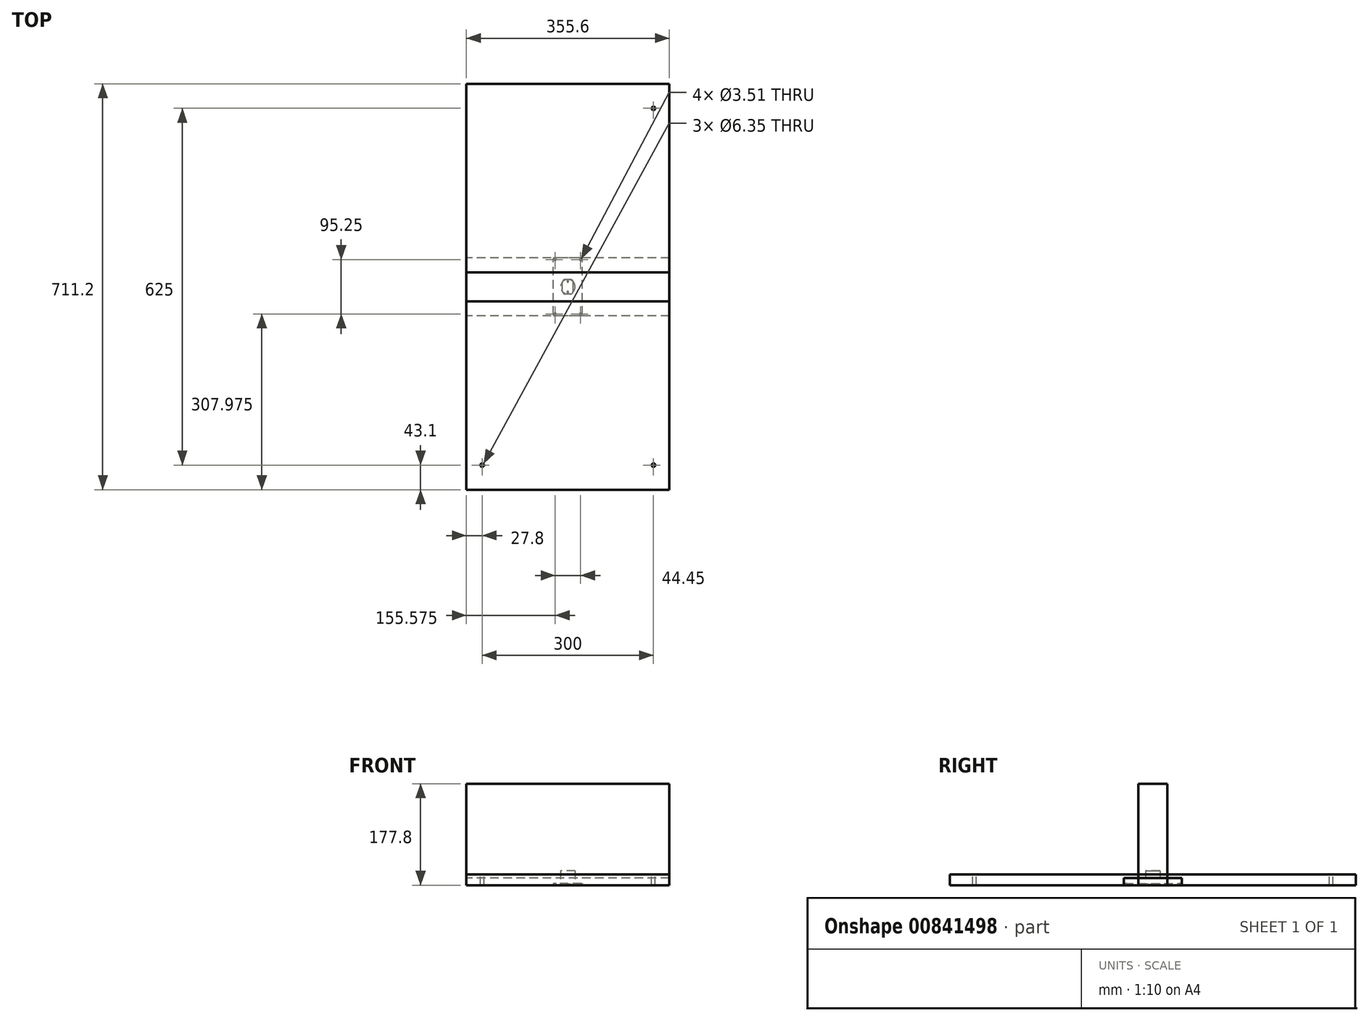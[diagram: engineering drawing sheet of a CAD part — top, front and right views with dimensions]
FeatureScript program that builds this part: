
annotation { "Feature Type Name" : "Feature", "Feature Type Description" : "" }
export const myFeature = defineFeature(function(context is Context, id is Id, definition is map)
    precondition{}
    {
        {
            var Q0;
            Q0=qCreatedBy(makeId("Top.planeOp"),FACE);
            var sketch = newSketch(context, id + "F0", { "sketchPlane" : qUnion([Q0])});
            skLineSegment(sketch, "E0.bottom", {"start": v(177.8, -355.6) * mm, "end": v(-177.8, -355.6) * mm});
            skLineSegment(sketch, "E0.top", {"start": v(177.8, 355.6) * mm, "end": v(-177.8, 355.6) * mm});
            skLineSegment(sketch, "E0.left", {"start": v(177.8, -355.6) * mm, "end": v(177.8, 355.6) * mm});
            skLineSegment(sketch, "E0.right", {"start": v(-177.8, -355.6) * mm, "end": v(-177.8, 355.6) * mm});
            skPoint(sketch, "E0.middle", {"position": v(0, 0) * mm});
            skSolve(sketch);
        }
        {
            var Q0;
            Q0=qSketchRegion(id+"F0",true);
            extrude(context, id + "F1", {"entities" : qUnion([Q0]), "depth" : 19.05 * mm, "offsetDistance" : 25.4 * mm});
        }
        {
            var Q0;
            Q0=qCreatedBy(makeId("Top.planeOp"),FACE);
            var sketch = newSketch(context, id + "F2", { "sketchPlane" : qUnion([Q0])});
            skLineSegment(sketch, "E1.bottom", {"start": v(177.8, -25.4) * mm, "end": v(-177.8, -25.4) * mm});
            skLineSegment(sketch, "E1.top", {"start": v(177.8, 25.4) * mm, "end": v(-177.8, 25.4) * mm});
            skLineSegment(sketch, "E1.left", {"start": v(177.8, -25.4) * mm, "end": v(177.8, 25.4) * mm});
            skLineSegment(sketch, "E1.right", {"start": v(-177.8, -25.4) * mm, "end": v(-177.8, 25.4) * mm});
            skPoint(sketch, "E1.middle", {"position": v(0, 0) * mm});
            skSolve(sketch);
        }
        {
            var Q0;
            Q0=qSketchRegion(id+"F2",true);
            extrude(context, id + "F3", {"entities" : qUnion([Q0]), "depth" : 177.8 * mm, "offsetDistance" : 25.4 * mm});
        }
        {
            var Q0;
            Q0=qCreatedBy(makeId("Top.planeOp"),FACE);
            var sketch = newSketch(context, id + "F4", { "sketchPlane" : qUnion([Q0])});
            skLineSegment(sketch, "E2.bottom", {"start": v(177.8, -50.8) * mm, "end": v(-177.8, -50.8) * mm});
            skLineSegment(sketch, "E2.top", {"start": v(177.8, 50.8) * mm, "end": v(-177.8, 50.8) * mm});
            skLineSegment(sketch, "E2.left", {"start": v(177.8, -50.8) * mm, "end": v(177.8, 50.8) * mm});
            skLineSegment(sketch, "E2.right", {"start": v(-177.8, -50.8) * mm, "end": v(-177.8, 50.8) * mm});
            skPoint(sketch, "E2.middle", {"position": v(0, 0) * mm});
            skSolve(sketch);
        }
        {
            var Q0;
            Q0=qSketchRegion(id+"F4",true);
            extrude(context, id + "F5", {"entities" : qUnion([Q0]), "depth" : 12.7 * mm, "offsetDistance" : 25.4 * mm});
        }
        {
            var Q0;
            Q0=qCreatedBy(makeId("Top.planeOp"),FACE);
            var sketch = newSketch(context, id + "F6", { "sketchPlane" : qUnion([Q0])});
            skCircle(sketch, "E3", {"center": v(0, 0) * mm, "radius": 12.7 * mm});
            skSolve(sketch);
        }
        {
            var Q0;
            Q0=qSketchRegion(id+"F6",true);
            extrude(context, id + "F7", {"entities" : qUnion([Q0]), "depth" : 25.4 * mm, "offsetDistance" : 25.4 * mm});
        }
        {
            var Q0;
            Q0=makeQuery(id+"F1.opExtrude","CAP_FACE",FACE,{"disambiguationData":[OSD([sQuery(id+"F0.wireOp",EDGE,"E0.bottom"),sQuery(id+"F0.wireOp",EDGE,"E0.top"),sQuery(id+"F0.wireOp",EDGE,"E0.left"),sQuery(id+"F0.wireOp",EDGE,"E0.right")])],"isStart":false});
            var sketch = newSketch(context, id + "F8", { "sketchPlane" : qUnion([Q0])});
            skLineSegment(sketch, "E4.bottom", {"start": v(150, 312.5) * mm, "end": v(-150, 312.5) * mm, "construction": true});
            skLineSegment(sketch, "E4.top", {"start": v(150, -312.5) * mm, "end": v(-150, -312.5) * mm, "construction": true});
            skLineSegment(sketch, "E4.left", {"start": v(150, 312.5) * mm, "end": v(150, -312.5) * mm, "construction": true});
            skLineSegment(sketch, "E4.right", {"start": v(-150, 312.5) * mm, "end": v(-150, -312.5) * mm, "construction": true});
            skPoint(sketch, "E4.middle", {"position": v(0, 0) * mm});
            skSolve(sketch);
        }
        {
            var Q0;
            Q0=sQuery(id+"F8.wireOp",VERTEX,"E4.top.end");
            var Q1;
            Q1=sQuery(id+"F8.wireOp",VERTEX,"E4.top.start");
            var Q2;
            Q2=sQuery(id+"F8.wireOp",VERTEX,"E4.bottom.start");
            var Q3;
            Q3=makeQuery(id+"F1.opExtrude","SWEPT_BODY",BODY,{"disambiguationData":[OSD([sQuery(id+"F0.wireOp",EDGE,"E0.bottom"),sQuery(id+"F0.wireOp",EDGE,"E0.top"),sQuery(id+"F0.wireOp",EDGE,"E0.left"),sQuery(id+"F0.wireOp",EDGE,"E0.right")])]});
            hole(context, id + "F9", {"style" : HoleStyle.SIMPLE, "endStyle" : HoleEndStyle.THROUGH, "holeDiameter" : 6.35 * mm, "majorDiameter" : 6.35 * mm, "isTappedThrough" : true, "tappedDepth" : 12.7 * mm, "tapClearance" : 3, "locations" : qUnion([Q0, Q1, Q2]), "scope" : qUnion([Q3])});
        }
        {
            var Q0;
            Q0=qSketchRegion(id+"F0",true);
            var sketch = newSketch(context, id + "F10", { "sketchPlane" : qUnion([Q0])});
            skLineSegment(sketch, "E5.bottom", {"start": v(25.4, -50.8) * mm, "end": v(-25.4, -50.8) * mm});
            skLineSegment(sketch, "E5.top", {"start": v(25.4, 50.8) * mm, "end": v(-25.4, 50.8) * mm});
            skLineSegment(sketch, "E5.left", {"start": v(25.4, -50.8) * mm, "end": v(25.4, 50.8) * mm});
            skLineSegment(sketch, "E5.right", {"start": v(-25.4, -50.8) * mm, "end": v(-25.4, 50.8) * mm});
            skPoint(sketch, "E5.middle", {"position": v(0, 0) * mm});
            skSolve(sketch);
        }
        {
            var Q0;
            Q0=qSketchRegion(id+"F10",true);
            extrude(context, id + "F11", {"entities" : qUnion([Q0]), "depth" : 3.17 * mm, "offsetDistance" : 25.4 * mm});
        }
        {
            var Q0;
            Q0=makeQuery(id+"F11.opExtrude","SWEPT_EDGE",EDGE,{"disambiguationData":[OSD([sQuery(id+"F10.wireOp",EDGE,"E5.bottom"),sQuery(id+"F10.wireOp",EDGE,"E5.left")])]});
            var Q1;
            Q1=makeQuery(id+"F11.opExtrude","SWEPT_EDGE",EDGE,{"disambiguationData":[OSD([sQuery(id+"F10.wireOp",EDGE,"E5.bottom"),sQuery(id+"F10.wireOp",EDGE,"E5.right")])]});
            var Q2;
            Q2=makeQuery(id+"F11.opExtrude","SWEPT_EDGE",EDGE,{"disambiguationData":[OSD([sQuery(id+"F10.wireOp",EDGE,"E5.top"),sQuery(id+"F10.wireOp",EDGE,"E5.left")])]});
            var Q3;
            Q3=makeQuery(id+"F11.opExtrude","SWEPT_EDGE",EDGE,{"disambiguationData":[OSD([sQuery(id+"F10.wireOp",EDGE,"E5.top"),sQuery(id+"F10.wireOp",EDGE,"E5.right")])]});
            fillet(context, id + "F12", {"entities" : qUnion([Q0, Q1, Q2, Q3]), "radius" : 1.59 * mm, "tangentPropagation" : true, "allowEdgeOverflow" : false});
        }
        {
            var Q0;
            Q0=makeQuery(id+"F11.opExtrude","CAP_FACE",FACE,{"disambiguationData":[OSD([sQuery(id+"F10.wireOp",EDGE,"E5.bottom"),sQuery(id+"F10.wireOp",EDGE,"E5.top"),sQuery(id+"F10.wireOp",EDGE,"E5.left"),sQuery(id+"F10.wireOp",EDGE,"E5.right")])],"isStart":false});
            var sketch = newSketch(context, id + "F13", { "sketchPlane" : qUnion([Q0])});
            skLineSegment(sketch, "E6.bottom", {"start": v(-22.23, -47.62) * mm, "end": v(22.23, -47.62) * mm});
            skLineSegment(sketch, "E6.top", {"start": v(-22.23, 47.62) * mm, "end": v(22.23, 47.62) * mm});
            skLineSegment(sketch, "E6.left", {"start": v(-22.23, -47.62) * mm, "end": v(-22.23, 47.62) * mm});
            skLineSegment(sketch, "E6.right", {"start": v(22.23, -47.62) * mm, "end": v(22.23, 47.62) * mm});
            skPoint(sketch, "E6.middle", {"position": v(0, 0) * mm});
            skSolve(sketch);
        }
        {
            var Q0;
            Q0=sQuery(id+"F13.wireOp",VERTEX,"E6.bottom.end");
            var Q1;
            Q1=sQuery(id+"F13.wireOp",VERTEX,"E6.bottom.start");
            var Q2;
            Q2=sQuery(id+"F13.wireOp",VERTEX,"E6.left.end");
            var Q3;
            Q3=sQuery(id+"F13.wireOp",VERTEX,"E6.top.end");
            var Q4;
            Q4=makeQuery(id+"F11.opExtrude","SWEPT_BODY",BODY,{"disambiguationData":[OSD([sQuery(id+"F10.wireOp",EDGE,"E5.bottom"),sQuery(id+"F10.wireOp",EDGE,"E5.top"),sQuery(id+"F10.wireOp",EDGE,"E5.left"),sQuery(id+"F10.wireOp",EDGE,"E5.right")])]});
            hole(context, id + "F14", {"style" : HoleStyle.SIMPLE, "endStyle" : HoleEndStyle.THROUGH, "holeDiameter" : 3.5 * mm, "majorDiameter" : 6.35 * mm, "isTappedThrough" : true, "tappedDepth" : 12.7 * mm, "tapClearance" : 3, "locations" : qUnion([Q0, Q1, Q2, Q3]), "scope" : qUnion([Q4])});
        }
        {
            var Q0;
            Q0=qCreatedBy(makeId("Top.planeOp"),FACE);
            var sketch = newSketch(context, id + "F15", { "sketchPlane" : qUnion([Q0])});
            skLineSegment(sketch, "E7.bottom", {"start": v(9.53, -12.7) * mm, "end": v(-9.52, -12.7) * mm});
            skLineSegment(sketch, "E7.top", {"start": v(9.52, 12.7) * mm, "end": v(-9.53, 12.7) * mm});
            skLineSegment(sketch, "E7.left", {"start": v(9.53, -12.7) * mm, "end": v(9.52, 12.7) * mm});
            skLineSegment(sketch, "E7.right", {"start": v(-9.52, -12.7) * mm, "end": v(-9.53, 12.7) * mm});
            skPoint(sketch, "E7.middle", {"position": v(0, 0) * mm});
            skSolve(sketch);
        }
        {
            var Q0;
            Q0=qSketchRegion(id+"F15",true);
            extrude(context, id + "F16", {"entities" : qUnion([Q0]), "depth" : 1.59 * mm, "offsetDistance" : 25.4 * mm});
        }
        {
            var Q0;
            Q0=makeQuery(id+"F16.opExtrude","SWEPT_EDGE",EDGE,{"disambiguationData":[OSD([sQuery(id+"F15.wireOp",EDGE,"E7.bottom"),sQuery(id+"F15.wireOp",EDGE,"E7.left")])]});
            var Q1;
            Q1=makeQuery(id+"F16.opExtrude","SWEPT_EDGE",EDGE,{"disambiguationData":[OSD([sQuery(id+"F15.wireOp",EDGE,"E7.bottom"),sQuery(id+"F15.wireOp",EDGE,"E7.right")])]});
            var Q2;
            Q2=makeQuery(id+"F16.opExtrude","SWEPT_EDGE",EDGE,{"disambiguationData":[OSD([sQuery(id+"F15.wireOp",EDGE,"E7.top"),sQuery(id+"F15.wireOp",EDGE,"E7.left")])]});
            var Q3;
            Q3=makeQuery(id+"F16.opExtrude","SWEPT_EDGE",EDGE,{"disambiguationData":[OSD([sQuery(id+"F15.wireOp",EDGE,"E7.top"),sQuery(id+"F15.wireOp",EDGE,"E7.right")])]});
            fillet(context, id + "F17", {"entities" : qUnion([Q0, Q1, Q2, Q3]), "radius" : 5.08 * mm, "tangentPropagation" : true, "allowEdgeOverflow" : false});
        }
        {
            var Q0;
            Q0=makeQuery(id+"F16.opExtrude","CAP_FACE",FACE,{"disambiguationData":[OSD([sQuery(id+"F15.wireOp",EDGE,"E7.bottom"),sQuery(id+"F15.wireOp",EDGE,"E7.top"),sQuery(id+"F15.wireOp",EDGE,"E7.left"),sQuery(id+"F15.wireOp",EDGE,"E7.right")])],"isStart":false});
            var sketch = newSketch(context, id + "F18", { "sketchPlane" : qUnion([Q0])});
            skLineSegment(sketch, "E8.bottom", {"start": v(6.35, -9.53) * mm, "end": v(-6.35, -9.53) * mm});
            skLineSegment(sketch, "E8.top", {"start": v(6.35, 9.53) * mm, "end": v(-6.35, 9.53) * mm});
            skLineSegment(sketch, "E8.left", {"start": v(6.35, -9.53) * mm, "end": v(6.35, 9.53) * mm});
            skLineSegment(sketch, "E8.right", {"start": v(-6.35, -9.53) * mm, "end": v(-6.35, 9.53) * mm});
            skPoint(sketch, "E8.middle", {"position": v(0, 0) * mm});
            skPoint(sketch, "E9", {"position": v(-6.35, 0) * mm});
            skPoint(sketch, "E10", {"position": v(6.35, 0) * mm});
            skPoint(sketch, "E11", {"position": v(0, 9.53) * mm});
            skPoint(sketch, "E12", {"position": v(0, -9.53) * mm});
            skSolve(sketch);
        }
        {
            var Q0;
            Q0=sQuery(id+"F18.wireOp",VERTEX,"E11");
            var Q1;
            Q1=sQuery(id+"F18.wireOp",VERTEX,"E12");
            var Q2;
            Q2=makeQuery(id+"F16.opExtrude","SWEPT_BODY",BODY,{"disambiguationData":[OSD([sQuery(id+"F15.wireOp",EDGE,"E7.bottom"),sQuery(id+"F15.wireOp",EDGE,"E7.top"),sQuery(id+"F15.wireOp",EDGE,"E7.left"),sQuery(id+"F15.wireOp",EDGE,"E7.right")])]});
            hole(context, id + "F19", {"style" : HoleStyle.SIMPLE, "endStyle" : HoleEndStyle.THROUGH, "holeDiameter" : 2.84 * mm, "majorDiameter" : 6.35 * mm, "isTappedThrough" : true, "tappedDepth" : 12.7 * mm, "tapClearance" : 3, "locations" : qUnion([Q0, Q1]), "scope" : qUnion([Q2])});
        }
    });
